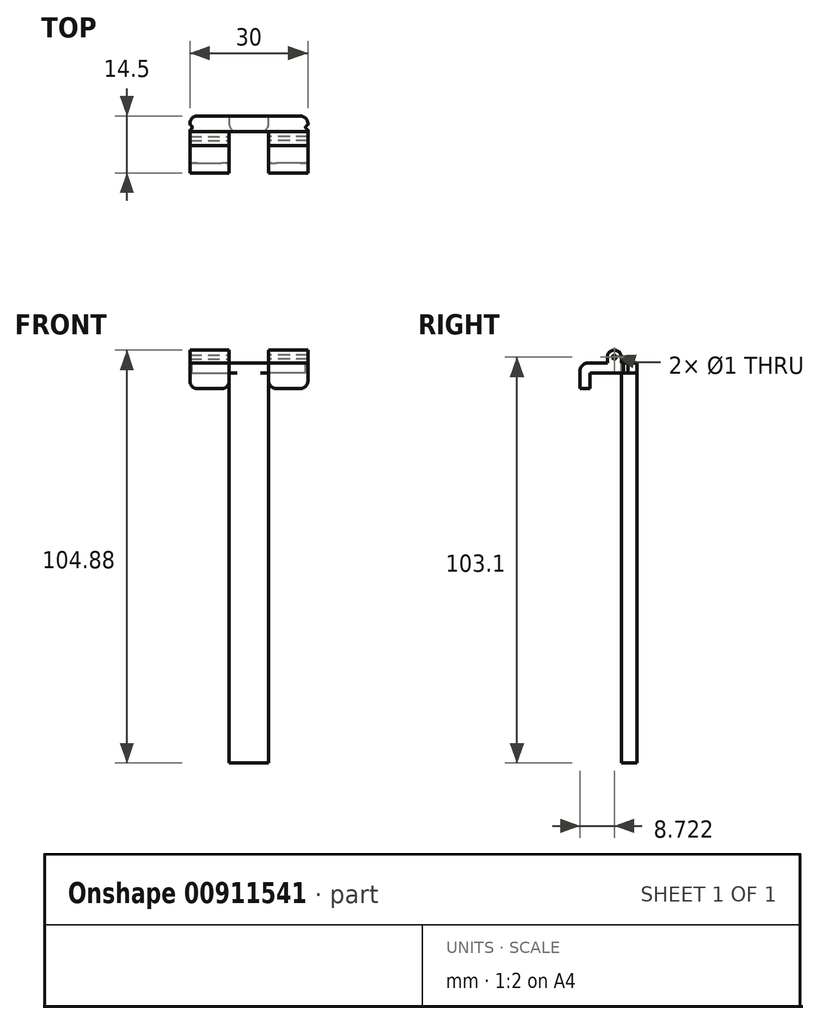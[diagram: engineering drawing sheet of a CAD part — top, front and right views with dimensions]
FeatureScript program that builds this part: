
annotation { "Feature Type Name" : "Feature", "Feature Type Description" : "" }
export const myFeature = defineFeature(function(context is Context, id is Id, definition is map)
    precondition{}
    {
        {
            var Q0;
            Q0=qCreatedBy(makeId("Top.planeOp"),FACE);
            var sketch = newSketch(context, id + "F0", { "sketchPlane" : qUnion([Q0])});
            skLineSegment(sketch, "E0.top", {"start": v(0, -4) * mm, "end": v(5, -4) * mm});
            skLineSegment(sketch, "E0.right", {"start": v(5, 0) * mm, "end": v(5, -4) * mm});
            skLineSegment(sketch, "E1", {"start": v(5, 0) * mm, "end": v(0, 0) * mm});
            skLineSegment(sketch, "E2", {"start": v(0, 0) * mm, "end": v(0, -4) * mm});
            skSolve(sketch);
        }
        {
            var Q0;
            Q0 = qSketchRegion(id + "F0", true);
            extrude(context, id + "F1", {"entities" : qUnion([Q0]), "oppositeDirection" : true, "depth" : 101.6 * mm, "offsetDistance" : 25 * mm});
        }
        {
            var Q0;
            Q0=makeQuery(id+"F1.opExtrude","SWEPT_FACE",FACE,{"disambiguationData":[OSD([sQuery(id+"F0.wireOp",EDGE,"E0.right")])]});
            var sketch = newSketch(context, id + "F2", { "sketchPlane" : qUnion([Q0])});
            skLineSegment(sketch, "E3", {"start": v(0, 0) * mm, "end": v(-4, 0) * mm});
            skLineSegment(sketch, "E4", {"start": v(-14.5, 0) * mm, "end": v(-14.5, -6.5) * mm});
            skLineSegment(sketch, "E5", {"start": v(-14.5, -6.5) * mm, "end": v(-12, -6.5) * mm});
            skLineSegment(sketch, "E6", {"start": v(-12, -6.5) * mm, "end": v(-12, -2.5) * mm});
            skLineSegment(sketch, "E7", {"start": v(-12, -2.5) * mm, "end": v(0, -2.5) * mm});
            skLineSegment(sketch, "E8", {"start": v(0, 0) * mm, "end": v(0, -2.5) * mm});
            skPoint(sketch, "E9.orphan", {"position": v(-4, -2.5) * mm});
            skCircle(sketch, "E10", {"center": v(-5.78, 1.5) * mm, "radius": 0.5 * mm});
            skLineSegment(sketch, "E11.left", {"start": v(-4, 0) * mm, "end": v(-4, 1.5) * mm});
            skLineSegment(sketch, "E11.right", {"start": v(-7.56, 0) * mm, "end": v(-7.56, 1.5) * mm});
            skArc(sketch, "E12", {"start": v(-4, 1.5) * mm, "mid": v(-5.78, 3.28) * mm, "end": v(-7.56, 1.5) * mm});
            skLineSegment(sketch, "E13", {"start": v(-7.56, 1.5) * mm, "end": v(-4, 1.5) * mm, "construction": true});
            skLineSegment(sketch, "E14.trimOffspring", {"start": v(-7.56, 0) * mm, "end": v(-14.5, 0) * mm});
            skSolve(sketch);
        }
        {
            var Q0;
            Q0 = qSketchRegion(id + "F2", true);
            extrude(context, id + "F3", {"entities" : qUnion([Q0]), "operationType" : NewBodyOperationType.ADD, "depth" : 10 * mm, "offsetDistance" : 25 * mm});
        }
        {
            var Q0;
            Q0=makeQuery(id+"F3.opExtrude","SWEPT_EDGE",EDGE,{"disambiguationData":[OSD([sQuery(id+"F2.wireOp",EDGE,"E4"),sQuery(id+"F2.wireOp",EDGE,"E14.trimOffspring")])]});
            var Q1;
            {var subQ0=sQuery(id+"F0.wireOp",EDGE,"E0.top");Q1=makeQuery(id+"F3.boolean.opBoolean","SPLIT",EDGE,{"disambiguationData":[topologyDisambiguationEdgeConnected([makeQuery(id+"F3.opExtrude","CAP_FACE",FACE,{"disambiguationData":[OSD([sQuery(id+"F2.wireOp",EDGE,"E3"),sQuery(id+"F2.wireOp",EDGE,"E4"),sQuery(id+"F2.wireOp",EDGE,"E5"),sQuery(id+"F2.wireOp",EDGE,"E6"),sQuery(id+"F2.wireOp",EDGE,"E7"),sQuery(id+"F2.wireOp",EDGE,"E8"),sQuery(id+"F2.wireOp",EDGE,"E10"),sQuery(id+"F2.wireOp",EDGE,"E11.left"),sQuery(id+"F2.wireOp",EDGE,"E11.right"),sQuery(id+"F2.wireOp",EDGE,"E12"),sQuery(id+"F2.wireOp",EDGE,"E14.trimOffspring")])],"isStart":true})])],"derivedFrom":makeQuery(id+"F1.opExtrude","SWEPT_EDGE",EDGE,{"disambiguationData":[OSD([subQ0,sQuery(id+"F0.wireOp",EDGE,"E0.right")])]})});}
            var Q2;
            Q2=makeQuery(id+"F3.opExtrude","CAP_EDGE",EDGE,{"disambiguationData":[OSD([sQuery(id+"F2.wireOp",EDGE,"E8")])],"isStart":false});
            var Q3;
            Q3=makeQuery(id+"F3.opExtrude","CAP_EDGE",EDGE,{"disambiguationData":[OSD([sQuery(id+"F2.wireOp",EDGE,"E5")])],"isStart":false});
            var Q4;
            Q4=makeQuery(id+"F3.opExtrude","CAP_EDGE",EDGE,{"disambiguationData":[OSD([sQuery(id+"F2.wireOp",EDGE,"E5")])],"isStart":true});
            fillet(context, id + "F4", {"entities" : qUnion([Q0, Q1, Q2, Q3, Q4]), "radius" : 2 * mm, "allowEdgeOverflow" : false});
        }
        {
            var Q0;
            Q0=makeQuery(id+"F3.opExtrude","SWEPT_EDGE",EDGE,{"disambiguationData":[OSD([sQuery(id+"F2.wireOp",EDGE,"E6"),sQuery(id+"F2.wireOp",EDGE,"E7")])]});
            fillet(context, id + "F5", {"entities" : qUnion([Q0]), "radius" : .5 * mm, "tangentPropagation" : true, "allowEdgeOverflow" : false});
        }
        {
            var Q0;
            Q0=makeQuery(id+"F3.boolean.opBoolean","MERGE",FACE,{"derivedFrom":[makeQuery(id+"F1.opExtrude","CAP_FACE",FACE,{"disambiguationData":[OSD([sQuery(id+"F0.wireOp",EDGE,"E0.top"),sQuery(id+"F0.wireOp",EDGE,"E0.right"),sQuery(id+"F0.wireOp",EDGE,"E1"),sQuery(id+"F0.wireOp",EDGE,"E2")])],"isStart":true}),makeQuery(id+"F3.opExtrude","SWEPT_FACE",FACE,{"disambiguationData":[OSD([sQuery(id+"F2.wireOp",EDGE,"E3")])]})]});
            var sketch = newSketch(context, id + "F6", { "sketchPlane" : qUnion([Q0])});
            skArc(sketch, "E15", {"start": v(15, -2.32) * mm, "mid": v(14.43, -2.9) * mm, "end": v(15, -3.46) * mm});
            skLineSegment(sketch, "E16", {"start": v(15, -4) * mm, "end": v(15, -2) * mm, "construction": true});
            skLineSegment(sketch, "E17", {"start": v(15, -2.32) * mm, "end": v(15, -3.46) * mm});
            skSolve(sketch);
        }
        {
            var Q0;
            Q0 = qSketchRegion(id + "F6", true);
            extrude(context, id + "F7", {"entities" : qUnion([Q0]), "operationType" : NewBodyOperationType.REMOVE, "endBound" : BoundingType.THROUGH_ALL, "oppositeDirection" : true, "depth" : 25 * mm, "offsetDistance" : 25 * mm});
        }
        {
            var Q0;
            Q0=makeQuery(id+"F1.opExtrude","SWEPT_BODY",BODY,{"disambiguationData":[OSD([sQuery(id+"F0.wireOp",EDGE,"E0.top"),sQuery(id+"F0.wireOp",EDGE,"E0.right"),sQuery(id+"F0.wireOp",EDGE,"E1"),sQuery(id+"F0.wireOp",EDGE,"E2")])]});
            var Q1;
            Q1=qCreatedBy(makeId("Right.planeOp"),FACE);
            mirror(context, id + "F8", {"operationType" : NewBodyOperationType.ADD, "entities" : qUnion([Q0]), "mirrorPlane" : qUnion([Q1])});
        }
    });
